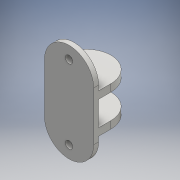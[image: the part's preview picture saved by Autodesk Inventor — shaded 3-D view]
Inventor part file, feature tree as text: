
AUTODESK INVENTOR PART (.ipt)
format: ipt  version: 2016 (Build 200138000, 138)  size: 138,240 bytes
history: native  units: mm
features: sketch x3, extrude x2, fillet x2, hole x1
ambient origin geometry x8: Origin, YZ Plane, XZ Plane, XY Plane, X Axis, Y Axis, Z Axis, Center Point
bodies: Solid1 (feature_tree)
feature tree (8):
  extrude  "Extrusion1"  Depth=20.0mm
  extrude  "Extrusion2"  Depth=3.0mm
  fillet  "Fillet1"  Radius=5.0mm
  hole  "Hole1"  [1 undecoded]
  fillet  "Fillet2"  Radius=5.0mm
  sketch  "Sketch1"  dims[d0=20.0mm d1=40.0mm]
  sketch  "Sketch3"  dims[d2=2.0mm d3=0.0mm d6=3.0mm d7=5.0mm]
  sketch  "Sketch4"  dims[d8=15.0mm d9=0.0mm d10=10.0mm d11=5.0mm d12=5.0mm d13=3.0mm d14=6.0mm d15=4.0mm d16=2.0mm d17=90.0deg d18=8.0mm d19=20.594885mm d20=10.0mm]
note: 1 required parameter value undecoded (feature->parameter linkage not recoverable at this tier; creation-order binding heuristic only, values carry confidence <= 0.55)
